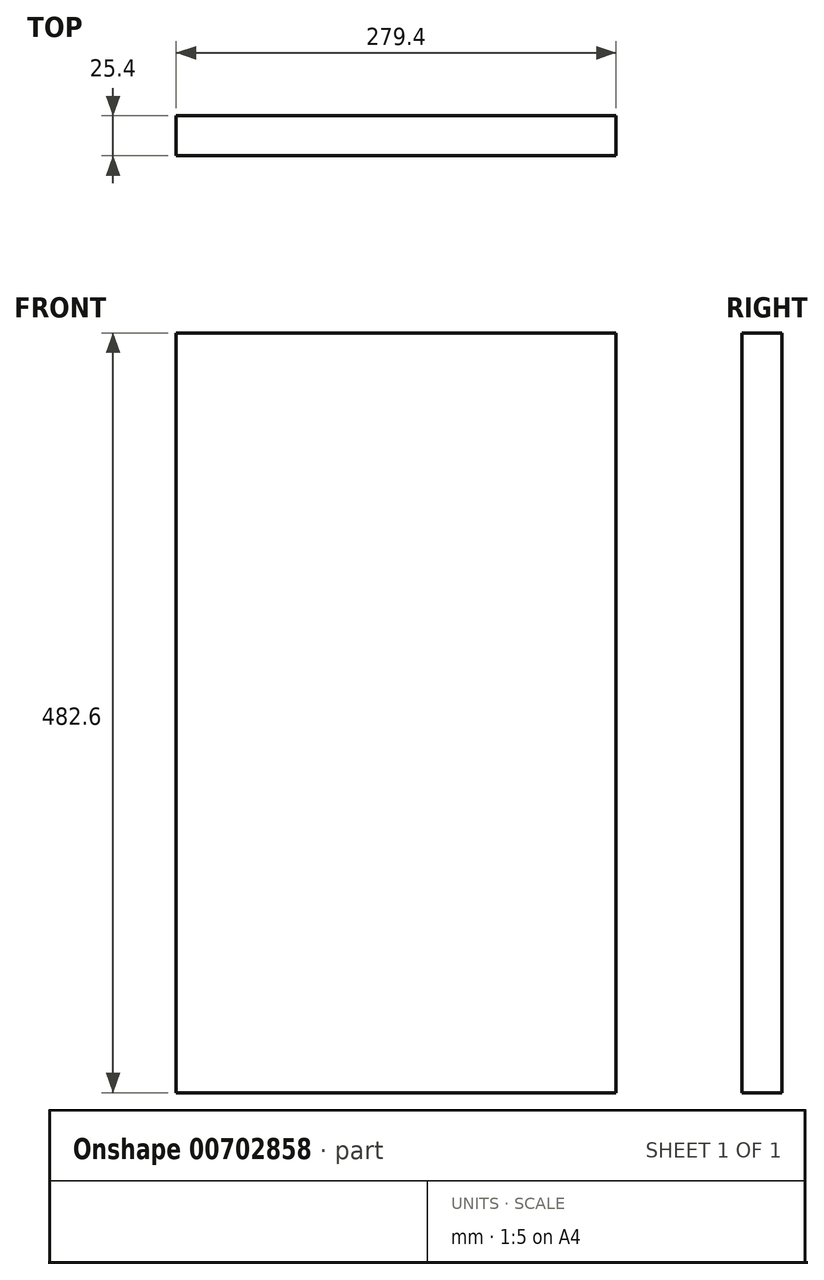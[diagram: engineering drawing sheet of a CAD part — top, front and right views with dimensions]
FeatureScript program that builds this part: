
annotation { "Feature Type Name" : "Feature", "Feature Type Description" : "" }
export const myFeature = defineFeature(function(context is Context, id is Id, definition is map)
    precondition{}
    {
        {
            var Q0;
            Q0=qCreatedBy(makeId("Front.planeOp"),FACE);
            var sketch = newSketch(context, id + "F0", { "sketchPlane" : qUnion([Q0])});
            skLineSegment(sketch, "E0.bottom", {"start": v(139.7, 241.3) * mm, "end": v(-139.7, 241.3) * mm});
            skLineSegment(sketch, "E0.top", {"start": v(139.7, -241.3) * mm, "end": v(-139.7, -241.3) * mm});
            skLineSegment(sketch, "E0.left", {"start": v(139.7, 241.3) * mm, "end": v(139.7, -241.3) * mm});
            skLineSegment(sketch, "E0.right", {"start": v(-139.7, 241.3) * mm, "end": v(-139.7, -241.3) * mm});
            skPoint(sketch, "E0.middle", {"position": v(0, 0) * mm});
            skSolve(sketch);
        }
        {
            var Q0;
            Q0=makeQuery(id+"F0.imprint","IMPRINT",FACE,{"disambiguationData":[TD([[makeQuery(id+"F0.imprint","IMPRINT",EDGE,{"derivedFrom":sQuery(id+"F0.wireOp",EDGE,"E0.bottom")}),1.0]])]});
            extrude(context, id + "F1", {"entities" : qUnion([Q0]), "depth" : 25.4 * mm, "offsetDistance" : 25.4 * mm});
        }
    });
